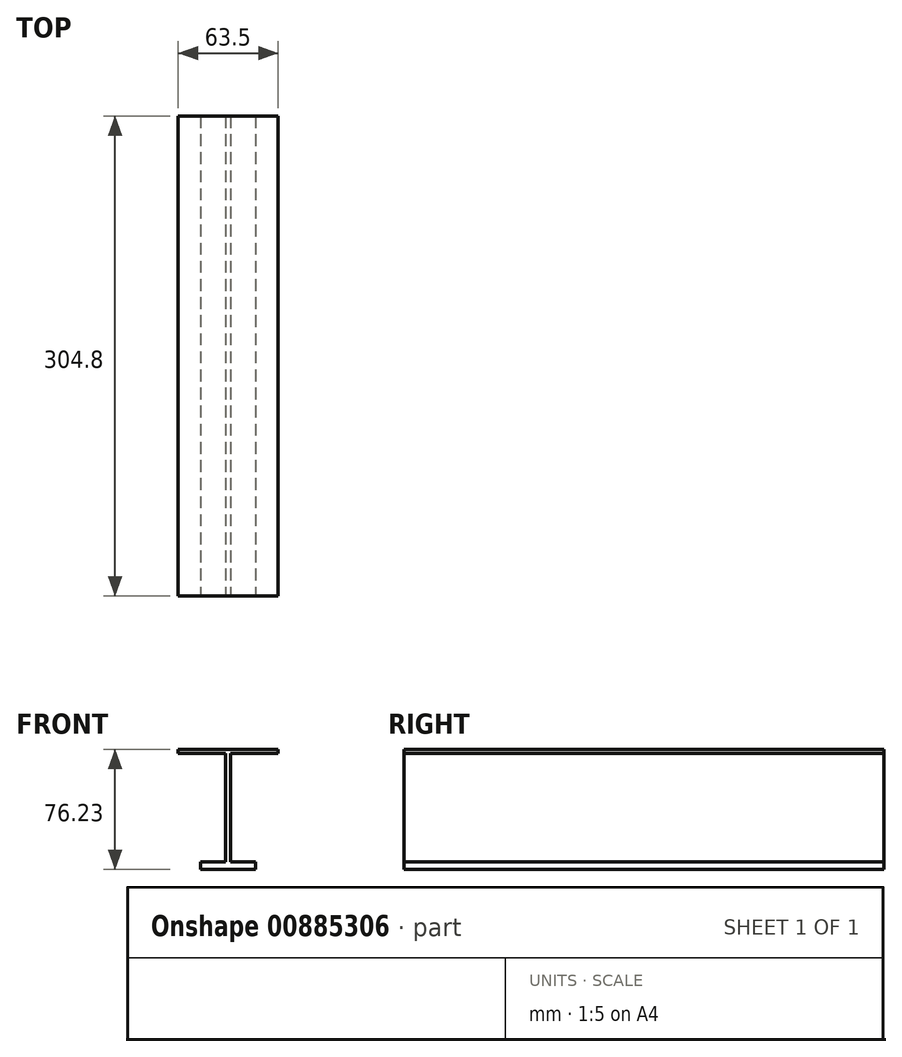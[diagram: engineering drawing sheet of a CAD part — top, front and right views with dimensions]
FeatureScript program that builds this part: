
annotation { "Feature Type Name" : "Feature", "Feature Type Description" : "" }
export const myFeature = defineFeature(function(context is Context, id is Id, definition is map)
    precondition{}
    {
        {
            var Q0;
            Q0=qCreatedBy(makeId("Front.planeOp"),FACE);
            var sketch = newSketch(context, id + "F0", { "sketchPlane" : qUnion([Q0])});
            skLineSegment(sketch, "E0.bottom", {"start": v(-1.59, 38.1) * mm, "end": v(1.59, 38.1) * mm});
            skLineSegment(sketch, "E0.top", {"start": v(-1.59, -38.1) * mm, "end": v(1.59, -38.1) * mm});
            skLineSegment(sketch, "E0.left", {"start": v(-1.59, 35.71) * mm, "end": v(-1.59, -33.3) * mm});
            skLineSegment(sketch, "E0.right", {"start": v(1.59, 35.71) * mm, "end": v(1.59, -33.3) * mm});
            skPoint(sketch, "E0.middle", {"position": v(0, 0) * mm});
            skLineSegment(sketch, "E1.bottom", {"start": v(-17.46, -33.3) * mm, "end": v(-1.59, -33.3) * mm});
            skLineSegment(sketch, "E1.top", {"start": v(-17.46, -38.13) * mm, "end": v(17.46, -38.13) * mm});
            skLineSegment(sketch, "E1.left", {"start": v(-17.46, -33.3) * mm, "end": v(-17.46, -38.13) * mm});
            skLineSegment(sketch, "E1.right", {"start": v(17.46, -33.3) * mm, "end": v(17.46, -38.13) * mm});
            skPoint(sketch, "E1.middle", {"position": v(0, -35.71) * mm});
            skLineSegment(sketch, "E2.bottom", {"start": v(-31.75, 35.71) * mm, "end": v(-1.59, 35.71) * mm});
            skLineSegment(sketch, "E2.top", {"start": v(-31.75, 38.1) * mm, "end": v(31.75, 38.1) * mm});
            skLineSegment(sketch, "E2.left", {"start": v(-31.75, 35.71) * mm, "end": v(-31.75, 38.1) * mm});
            skLineSegment(sketch, "E2.right", {"start": v(31.75, 35.71) * mm, "end": v(31.75, 38.1) * mm});
            skPoint(sketch, "E2.middle", {"position": v(0, 36.9) * mm});
            skPoint(sketch, "E2.middle.positionSnap0", {"position": v(0, 38.1) * mm});
            skPoint(sketch, "E2.centerSnap0", {"position": v(0, 38.1) * mm});
            skLineSegment(sketch, "E3.trimOffspring", {"start": v(1.59, -33.3) * mm, "end": v(17.46, -33.3) * mm});
            skLineSegment(sketch, "E4.trimOffspring", {"start": v(1.59, 35.71) * mm, "end": v(31.75, 35.71) * mm});
            skSolve(sketch);
        }
        {
            var Q0;
            Q0=makeQuery(id+"F0.imprint","IMPRINT",FACE,{"disambiguationData":[TD([[makeQuery(id+"F0.imprint","IMPRINT",EDGE,{"derivedFrom":sQuery(id+"F0.wireOp",EDGE,"E0.left")}),1.0]])]});
            extrude(context, id + "F1", {"entities" : qUnion([Q0]), "oppositeDirection" : true, "depth" : 304.8 * mm, "offsetDistance" : 25.4 * mm});
        }
    });
